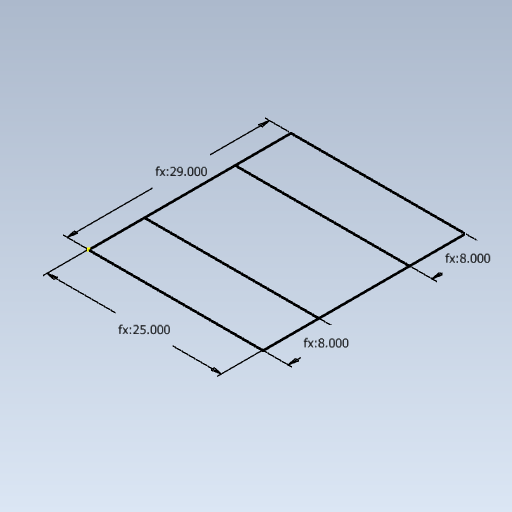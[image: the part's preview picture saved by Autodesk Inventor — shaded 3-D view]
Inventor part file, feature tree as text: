
AUTODESK INVENTOR PART (.ipt)
format: ipt  version: 2020 (Build 240168000, 168)  size: 83,968 bytes
history: native  units: in
note: dims shown in document units (in); Inventor stores cm internally (conversion verified against a paired STEP export)
features: other x1, sketch x1
ambient origin geometry x8: Origin, YZ Plane, XZ Plane, XY Plane, X Axis, Y Axis, Z Axis, Center Point
feature tree (2):
  parser-record x1  (decoder bookkeeping rows leaked as tree rows — omitted from the tree; the rows remain in map.json)
  sketch  "Sketch1"  dims[d5=8.0in d6=8.0in d7=25.0in d8=29.0in]
note: 1 file-system path scrubbed to <path> (originals preserved in map.json)
